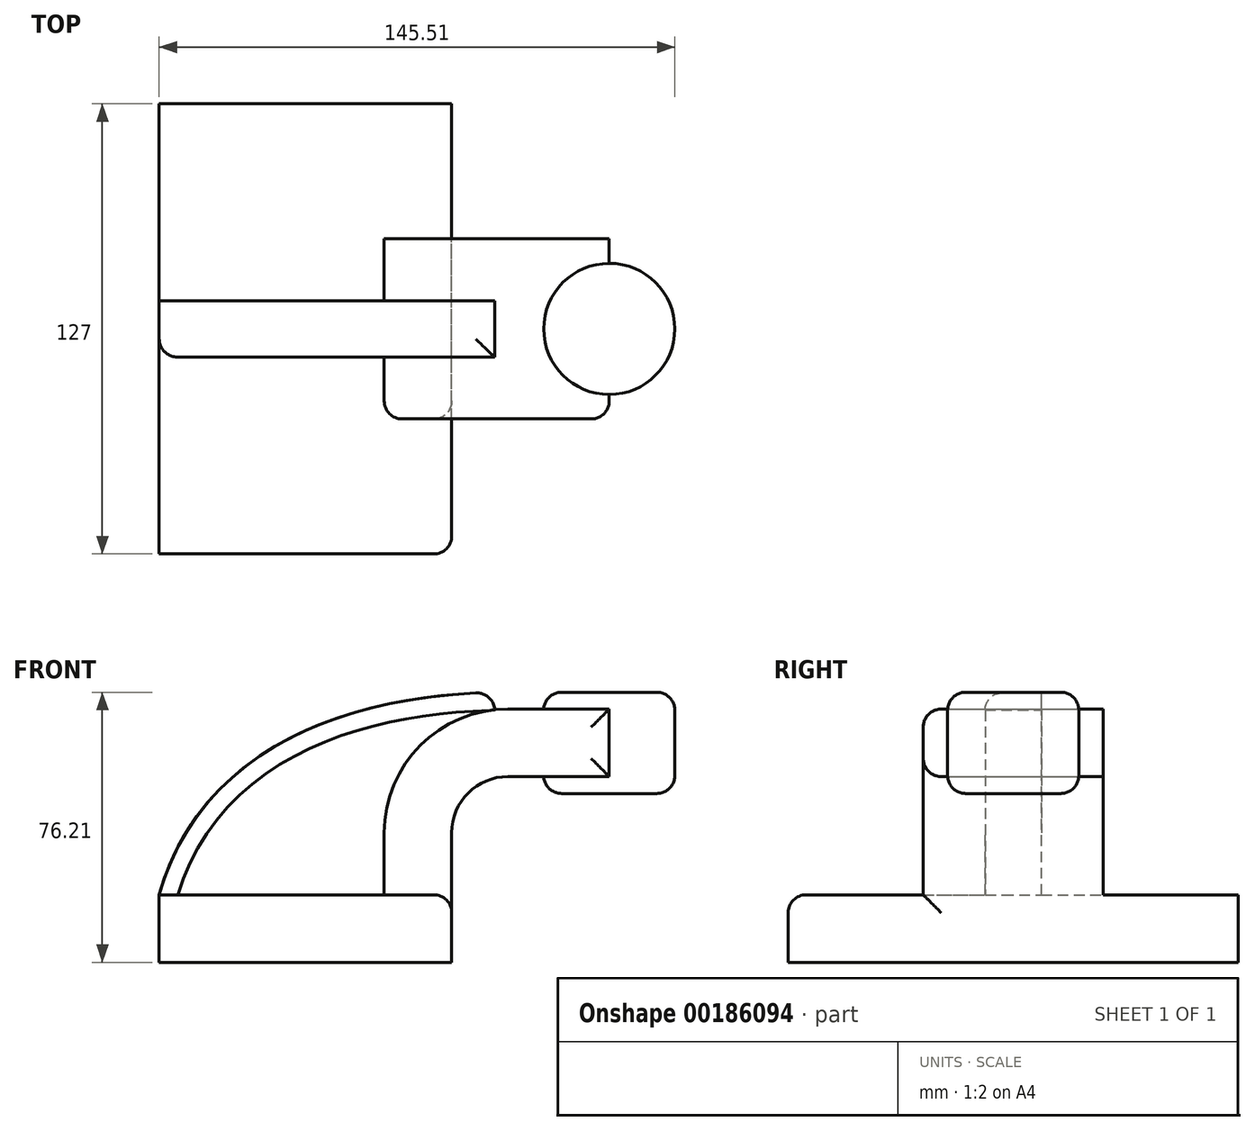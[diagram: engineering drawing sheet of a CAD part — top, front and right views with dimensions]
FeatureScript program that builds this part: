
annotation { "Feature Type Name" : "Feature", "Feature Type Description" : "" }
export const myFeature = defineFeature(function(context is Context, id is Id, definition is map)
    precondition{}
    {
        {
            var Q0;
            Q0=qCreatedBy(makeId("Front.planeOp"),FACE);
            var sketch = newSketch(context, id + "F0", { "sketchPlane" : qUnion([Q0])});
            skLineSegment(sketch, "E0.bottom", {"start": v(41.28, -9.52) * mm, "end": v(-41.27, -9.53) * mm});
            skLineSegment(sketch, "E0.top", {"start": v(41.27, 9.53) * mm, "end": v(-41.28, 9.53) * mm});
            skLineSegment(sketch, "E0.left", {"start": v(41.28, -9.52) * mm, "end": v(41.28, 9.53) * mm});
            skLineSegment(sketch, "E0.right", {"start": v(-41.27, -9.53) * mm, "end": v(-41.28, 9.53) * mm});
            skPoint(sketch, "E0.middle", {"position": v(0, 0) * mm});
            skLineSegment(sketch, "E1.bottom", {"start": v(104.23, 38.1) * mm, "end": v(53.43, 38.1) * mm});
            skLineSegment(sketch, "E1.top", {"start": v(104.23, 66.68) * mm, "end": v(53.43, 66.68) * mm});
            skLineSegment(sketch, "E1.left", {"start": v(104.23, 38.1) * mm, "end": v(104.23, 66.68) * mm});
            skLineSegment(sketch, "E1.right", {"start": v(53.43, 38.1) * mm, "end": v(53.43, 66.68) * mm});
            skPoint(sketch, "E1.middle", {"position": v(78.83, 52.39) * mm});
            skLineSegment(sketch, "E2", {"start": v(41.27, 9.53) * mm, "end": v(41.27, 27) * mm});
            skArc(sketch, "E3", {"start": v(41.27, 27) * mm, "mid": v(45.92, 38.23) * mm, "end": v(57.15, 42.88) * mm});
            skLineSegment(sketch, "E4", {"start": v(57.15, 42.88) * mm, "end": v(85.73, 42.88) * mm});
            skLineSegment(sketch, "E5.0", {"start": v(57.15, 61.93) * mm, "end": v(85.73, 61.93) * mm});
            skArc(sketch, "E5.1", {"start": v(22.23, 27) * mm, "mid": v(32.45, 51.7) * mm, "end": v(57.15, 61.93) * mm});
            skLineSegment(sketch, "E5.2", {"start": v(22.22, 9.53) * mm, "end": v(22.22, 27) * mm});
            skLineSegment(sketch, "E6", {"start": v(85.73, 66.68) * mm, "end": v(85.73, 38.1) * mm});
            skFitSpline(sketch, "E7", {"points": [v(-41.28, 9.53) * mm, v(53.43, 66.68) * mm], "startDerivative": vector(28.8, 101.95) * mm, "endDerivative": vector(160.3, 4.14) * mm});
            skSolve(sketch);
        }
        {
            var Q0;
            Q0=makeQuery(id+"F0.imprint","IMPRINT",FACE,{"disambiguationData":[TD([[makeQuery(id+"F0.imprint","IMPRINT",EDGE,{"derivedFrom":sQuery(id+"F0.wireOp",EDGE,"E0.bottom")}),-1.0]])]});
            extrude(context, id + "F1", {"entities" : qUnion([Q0]), "endBound" : BoundingType.SYMMETRIC, "depth" : 127 * mm});
        }
        {
            var Q0;
            {var subQ1=sQuery(id+"F0.wireOp",EDGE,"E2");Q0=makeQuery(id+"F0.imprint","IMPRINT",FACE,{"disambiguationData":[TD([[makeQuery(id+"F0.imprint","IMPRINT",EDGE,{"derivedFrom":subQ1}),1.0]])]});}
            var Q1;
            {var subQ1=sQuery(id+"F0.wireOp",EDGE,"E4");Q1=makeQuery(id+"F0.imprint","IMPRINT",FACE,{"disambiguationData":[TD([[makeQuery(id+"F0.imprint","IMPRINT",EDGE,{"derivedFrom":subQ1}),1.0]])]});}
            extrude(context, id + "F2", {"entities" : qUnion([Q0, Q1]), "operationType" : NewBodyOperationType.ADD, "endBound" : BoundingType.SYMMETRIC, "depth" : 50.8 * mm});
        }
        {
            var Q0;
            {var subQ0=sQuery(id+"F0.wireOp",EDGE,"E5.2");Q0=makeQuery(id+"F0.imprint","IMPRINT",FACE,{"disambiguationData":[TD([[makeQuery(id+"F0.imprint","IMPRINT",EDGE,{"derivedFrom":subQ0}),1.0]])]});}
            extrude(context, id + "F3", {"entities" : qUnion([Q0]), "operationType" : NewBodyOperationType.ADD, "endBound" : BoundingType.SYMMETRIC, "depth" : 15.88 * mm});
        }
        {
            var Q0;
            {var subQ0=sQuery(id+"F0.wireOp",EDGE,"E1.left");Q0=makeQuery(id+"F0.imprint","IMPRINT",FACE,{"disambiguationData":[TD([[makeQuery(id+"F0.imprint","IMPRINT",EDGE,{"derivedFrom":subQ0}),1.0]])]});}
            var Q1;
            Q1=sQuery(id+"F0.wireOp",EDGE,"E6");
            revolve(context, id + "F4", {"operationType" : NewBodyOperationType.ADD, "entities" : qUnion([Q0]), "axis" : qUnion([Q1]), "revolveType" : RevolveType.FULL});
        }
        {
            var Q0;
            Q0=makeQuery(id+"F1.opExtrude","CAP_EDGE",EDGE,{"disambiguationData":[OSD([sQuery(id+"F0.wireOp",EDGE,"E0.left")])],"isStart":false});
            var Q1;
            Q1=makeQuery(id+"F1.opExtrude","CAP_EDGE",EDGE,{"disambiguationData":[OSD([sQuery(id+"F0.wireOp",EDGE,"E0.top")])],"isStart":false});
            var Q2;
            {var subQ0=sQuery(id+"F0.wireOp",EDGE,"E2");var subQ1=sQuery(id+"F0.wireOp",EDGE,"E0.top");var subQ2=sQuery(id+"F0.wireOp",EDGE,"E0.left");Q2=makeQuery(id+"F2.boolean.opBoolean","SPLIT",EDGE,{"disambiguationData":[TD([makeQuery(id+"F1.opExtrude","CAP_FACE",FACE,{"disambiguationData":[OSD([sQuery(id+"F0.wireOp",EDGE,"E0.bottom"),subQ1,subQ2,sQuery(id+"F0.wireOp",EDGE,"E0.right")])],"isStart":false})])],"derivedFrom":makeQuery(id+"F1.opExtrude","SWEPT_EDGE",EDGE,{"disambiguationData":[OSD([subQ1,subQ2,subQ0])]})});}
            var Q3;
            Q3=makeQuery(id+"F2.opExtrude","CAP_EDGE",EDGE,{"disambiguationData":[OSD([sQuery(id+"F0.wireOp",EDGE,"E2")])],"isStart":false});
            var Q4;
            Q4=makeQuery(id+"F2.opExtrude","CAP_EDGE",EDGE,{"disambiguationData":[OSD([sQuery(id+"F0.wireOp",EDGE,"E5.2")])],"isStart":false});
            var Q5;
            Q5=makeQuery(id+"F2.opExtrude","CAP_EDGE",EDGE,{"disambiguationData":[OSD([sQuery(id+"F0.wireOp",EDGE,"E6")])],"isStart":false});
            var Q6;
            Q6=makeQuery(id+"F4.opRevolve","SWEPT_EDGE",EDGE,{"disambiguationData":[OSD([sQuery(id+"F0.wireOp",EDGE,"E1.top"),sQuery(id+"F0.wireOp",EDGE,"E1.left")])]});
            var Q7;
            Q7=makeQuery(id+"F4.opRevolve","SWEPT_EDGE",EDGE,{"disambiguationData":[OSD([sQuery(id+"F0.wireOp",EDGE,"E1.bottom"),sQuery(id+"F0.wireOp",EDGE,"E1.left")])]});
            var Q8;
            Q8=makeQuery(id+"F3.opExtrude","SWEPT_EDGE",EDGE,{"disambiguationData":[OSD([sQuery(id+"F0.wireOp",EDGE,"E1.top"),sQuery(id+"F0.wireOp",EDGE,"E1.right"),sQuery(id+"F0.wireOp",EDGE,"E7")])]});
            var Q9;
            Q9=makeQuery(id+"F3.opExtrude","CAP_EDGE",EDGE,{"disambiguationData":[OSD([sQuery(id+"F0.wireOp",EDGE,"E7")])],"isStart":false});
            fillet(context, id + "F5", {"entities" : qUnion([Q0, Q1, Q2, Q3, Q4, Q5, Q6, Q7, Q8, Q9]), "radius" : 5.08 * mm, "tangentPropagation" : true, "allowEdgeOverflow" : false});
        }
    });
